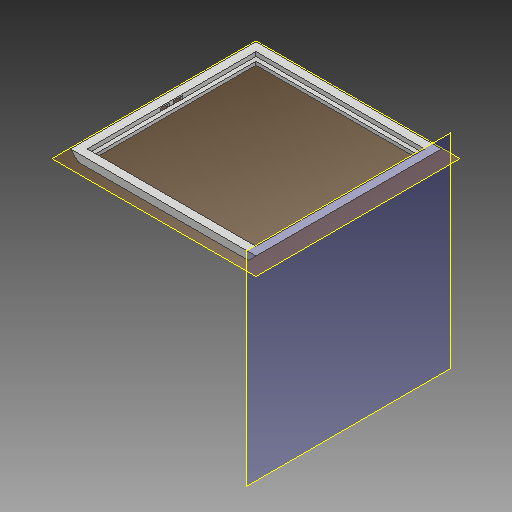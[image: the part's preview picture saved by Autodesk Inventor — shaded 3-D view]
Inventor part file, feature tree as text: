
AUTODESK INVENTOR PART (.ipt)
format: ipt  version: 2018.3 (Build 223284000, 284)  size: 206,336 bytes
history: native  units: mm
features: reference x20, other x12, extrude x6, sketch x6, plane x2, chamfer x1, projected_geometry x1
ambient origin geometry x8: Origin, YZ Plane, XZ Plane, XY Plane, X Axis, Y Axis, Z Axis, Center Point
bodies: Volumenkörper1 (feature_tree)
feature tree (48):
  extrude  "Extrusion1"  [1 undecoded]
  plane  "Arbeitsebene1"
  extrude  "Extrusion2"  Depth=10.0mm
  extrude  "Extrusion3"  Depth=10.0mm
  plane  "Arbeitsebene3"
  extrude  "Extrusion4"  Depth=8.0mm TaperAngle=0.0deg
  extrude  "Extrusion5"  Depth=2.0mm TaperAngle=0.0deg
  extrude  "Extrusion6"  Depth=18.0mm TaperAngle=45.0deg
  chamfer  "Fase2"  [1 undecoded]
  sketch  "Skizze1"  dims[d0=18.0mm d1=0.0mm d5=-20.0mm]
  reference  "Referenz1"
  reference  "Referenz2"
  reference  "Referenz3"
  reference  "Referenz4"
  reference  "Referenz5"
  sketch  "Skizze3"  dims[d6=17.0mm d7=0.0mm d8=10.0mm]
  reference  "Referenz12"
  reference  "Referenz13"
  reference  "Referenz14"
  reference  "Referenz15"
  reference  "Referenz16"
  reference  "Referenz17"
  reference  "Referenz18"
  reference  "Referenz19"
  sketch  "Skizze5"  dims[d9=10.0mm d10=10.0mm]
  sketch  "Skizze6"  dims[d11=10.0mm d12=8.0mm d13=0.0mm]
  reference  "Referenz20"
  reference  "Referenz21"
  reference  "Referenz22"
  reference  "Referenz23"
  reference  "Referenz24"
  reference  "Referenz25"
  sketch  "Skizze7"  dims[d14=25.0mm d15=0.0mm d16=2.0mm d17=0.0mm]
  projected_geometry  "Projizierte Kontur1"
  sketch  "Skizze8"  dims[d18=2.0mm d19=0.0mm d20=18.0mm d21=2.0mm d22=45.0deg]
  reference  "Referenz26"
  parser-record x2  (decoder bookkeeping rows leaked as tree rows — omitted from the tree; the rows remain in map.json)
  other  "SmartCube_Quadratisch.iam"
  other  "Wand2_MIR:1"
  other  "Wand1:1"
  other  "Wand1_MIR:1"
  other  "Wand2:1"
  other  "PV_Modul:1"
  other  "<userpath>\Documents\Dipl\Smartcube_Construction\Version_3\Baugruppe1.iam"
  other  "Baugruppe1.iam"
  other  "PV_Ramen_CPY_3_2:1"
  other  "PV_Modul_CPY_3_CPY2:1"
note: 2 required parameter values undecoded (feature->parameter linkage not recoverable at this tier; creation-order binding heuristic only, values carry confidence <= 0.55)
note: 2 file-system paths scrubbed to <path> (originals preserved in map.json)
